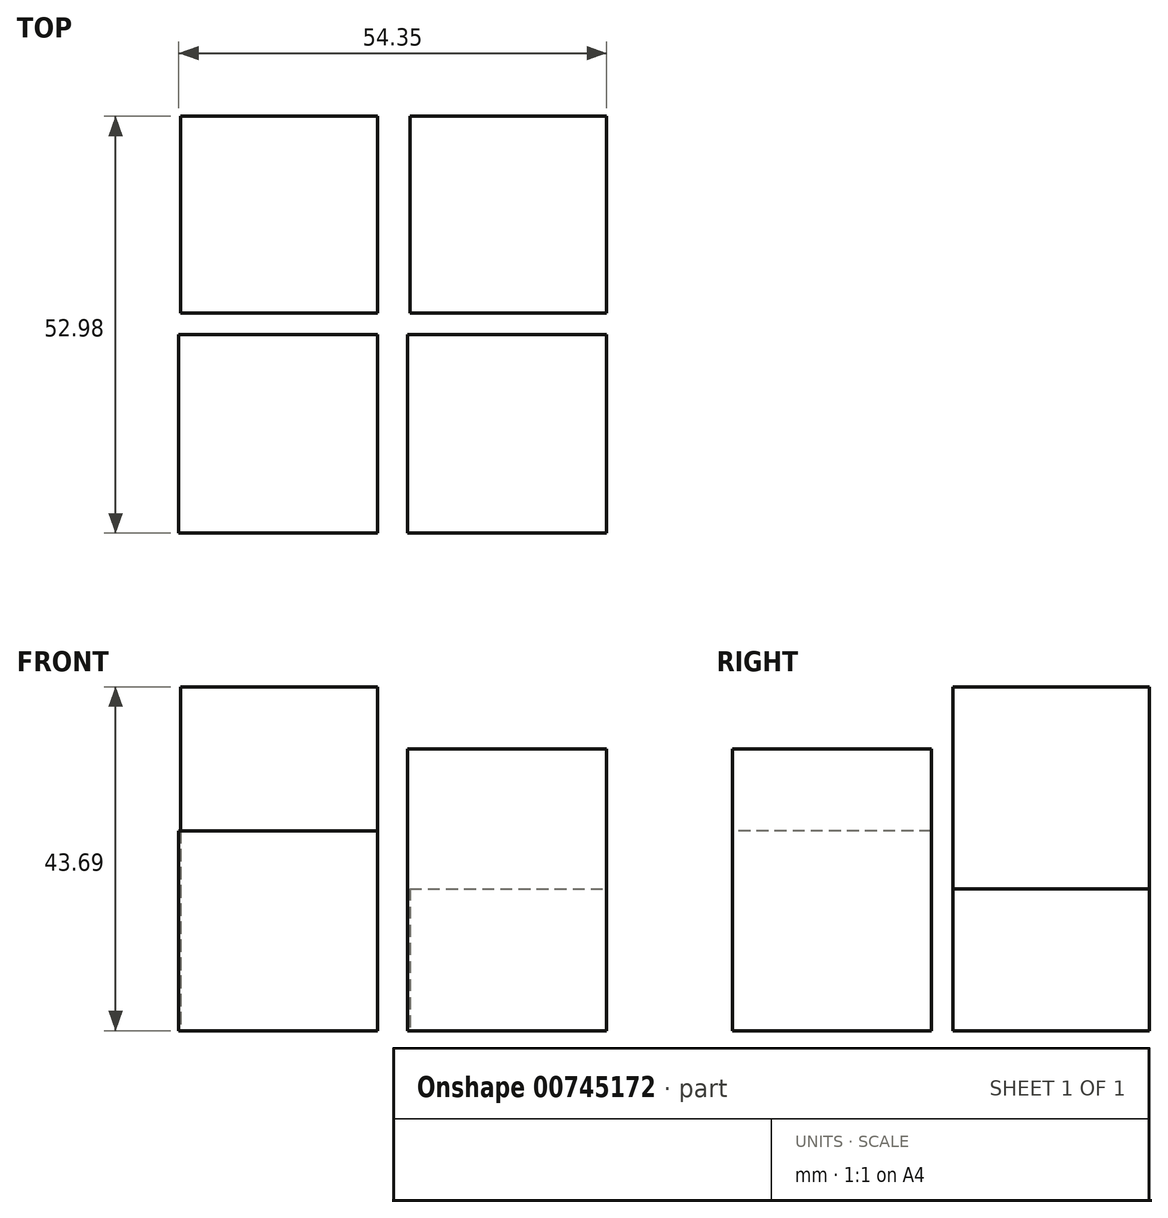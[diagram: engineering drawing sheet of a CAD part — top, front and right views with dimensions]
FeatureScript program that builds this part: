
annotation { "Feature Type Name" : "Feature", "Feature Type Description" : "" }
export const myFeature = defineFeature(function(context is Context, id is Id, definition is map)
    precondition{}
    {
        {
            var Q0;
            Q0=qCreatedBy(makeId("Top.planeOp"),FACE);
            var sketch = newSketch(context, id + "F0", { "sketchPlane" : qUnion([Q0])});
            skLineSegment(sketch, "E0.bottom", {"start": v(-44.95, 43.3) * mm, "end": v(-19.97, 43.3) * mm});
            skLineSegment(sketch, "E0.top", {"start": v(-44.95, 18.32) * mm, "end": v(-19.97, 18.32) * mm});
            skLineSegment(sketch, "E0.left", {"start": v(-44.95, 43.3) * mm, "end": v(-44.95, 18.32) * mm});
            skLineSegment(sketch, "E0.right", {"start": v(-19.97, 43.3) * mm, "end": v(-19.97, 18.32) * mm});
            skLineSegment(sketch, "E1.bottom", {"start": v(-15.85, 43.3) * mm, "end": v(9.13, 43.3) * mm});
            skLineSegment(sketch, "E1.top", {"start": v(-15.85, 18.32) * mm, "end": v(9.13, 18.32) * mm});
            skLineSegment(sketch, "E1.left", {"start": v(-15.85, 43.3) * mm, "end": v(-15.85, 18.32) * mm});
            skLineSegment(sketch, "E1.right", {"start": v(9.13, 43.3) * mm, "end": v(9.13, 18.32) * mm});
            skLineSegment(sketch, "E2.bottom", {"start": v(-45.22, 15.58) * mm, "end": v(-19.97, 15.58) * mm});
            skLineSegment(sketch, "E2.top", {"start": v(-45.22, -9.68) * mm, "end": v(-19.97, -9.68) * mm});
            skLineSegment(sketch, "E2.left", {"start": v(-45.22, 15.58) * mm, "end": v(-45.22, -9.68) * mm});
            skLineSegment(sketch, "E2.right", {"start": v(-19.97, 15.58) * mm, "end": v(-19.97, -9.68) * mm});
            skLineSegment(sketch, "E3.bottom", {"start": v(-16.13, 15.58) * mm, "end": v(9.13, 15.58) * mm});
            skLineSegment(sketch, "E3.top", {"start": v(-16.13, -9.68) * mm, "end": v(9.13, -9.68) * mm});
            skLineSegment(sketch, "E3.left", {"start": v(-16.13, 15.58) * mm, "end": v(-16.13, -9.68) * mm});
            skLineSegment(sketch, "E3.right", {"start": v(9.13, 15.58) * mm, "end": v(9.13, -9.68) * mm});
            skSolve(sketch);
        }
        {
            var Q0;
            Q0=makeQuery(id+"F0.imprint","IMPRINT",FACE,{"disambiguationData":[TD([[makeQuery(id+"F0.imprint","IMPRINT",EDGE,{"derivedFrom":sQuery(id+"F0.wireOp",EDGE,"E1.bottom")}),-1.0]])]});
            extrude(context, id + "F1", {"entities" : qUnion([Q0]), "depth" : 18.03 * mm, "offsetDistance" : 25.4 * mm});
        }
        {
            var Q0;
            Q0=makeQuery(id+"F0.imprint","IMPRINT",FACE,{"disambiguationData":[TD([[makeQuery(id+"F0.imprint","IMPRINT",EDGE,{"derivedFrom":sQuery(id+"F0.wireOp",EDGE,"E0.bottom")}),-1.0]])]});
            extrude(context, id + "F2", {"entities" : qUnion([Q0]), "depth" : 43.69 * mm, "offsetDistance" : 25.4 * mm});
        }
        {
            var Q0;
            Q0=makeQuery(id+"F0.imprint","IMPRINT",FACE,{"disambiguationData":[TD([[makeQuery(id+"F0.imprint","IMPRINT",EDGE,{"derivedFrom":sQuery(id+"F0.wireOp",EDGE,"E0.bottom")}),-1.0]])]});
            var Q1;
            Q1=makeQuery(id+"F0.imprint","IMPRINT",FACE,{"disambiguationData":[TD([[makeQuery(id+"F0.imprint","IMPRINT",EDGE,{"derivedFrom":sQuery(id+"F0.wireOp",EDGE,"E2.bottom")}),-1.0]])]});
            extrude(context, id + "F3", {"entities" : qUnion([Q0, Q1]), "operationType" : NewBodyOperationType.ADD, "depth" : 25.4 * mm, "offsetDistance" : 25.4 * mm});
        }
        {
            var Q0;
            Q0=makeQuery(id+"F0.imprint","IMPRINT",FACE,{"disambiguationData":[TD([[makeQuery(id+"F0.imprint","IMPRINT",EDGE,{"derivedFrom":sQuery(id+"F0.wireOp",EDGE,"E3.bottom")}),-1.0]])]});
            extrude(context, id + "F4", {"entities" : qUnion([Q0]), "depth" : 35.81 * mm, "offsetDistance" : 25.4 * mm});
        }
    });
